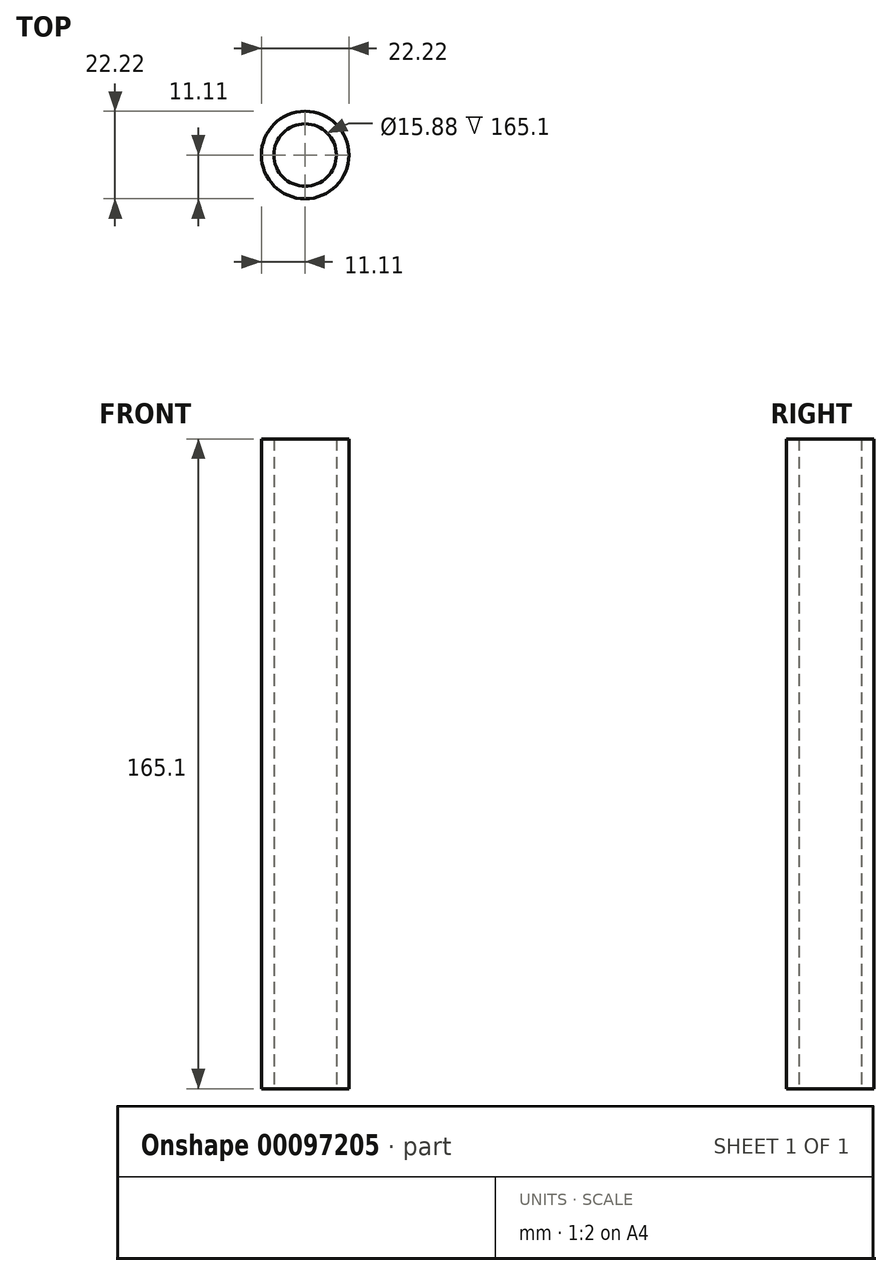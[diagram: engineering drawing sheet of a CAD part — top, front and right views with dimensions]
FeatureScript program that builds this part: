
annotation { "Feature Type Name" : "Feature", "Feature Type Description" : "" }
export const myFeature = defineFeature(function(context is Context, id is Id, definition is map)
    precondition{}
    {
        {
            var Q0;
            Q0=qCreatedBy(makeId("Top.planeOp"),FACE);
            var sketch = newSketch(context, id + "F0", { "sketchPlane" : qUnion([Q0])});
            skCircle(sketch, "E0", {"center": v(0, 0) * mm, "radius": 11.11 * mm});
            skCircle(sketch, "E1.0", {"center": v(0, 0) * mm, "radius": 7.94 * mm});
            skSolve(sketch);
        }
        {
            var Q0;
            Q0=makeQuery(id+"F0.imprint","IMPRINT",FACE,{"disambiguationData":[TD([[makeQuery(id+"F0.imprint","IMPRINT",EDGE,{"derivedFrom":sQuery(id+"F0.wireOp",EDGE,"E0")}),1.0]])]});
            extrude(context, id + "F1", {"entities" : qUnion([Q0]), "depth" : 165.1 * mm});
        }
    });
